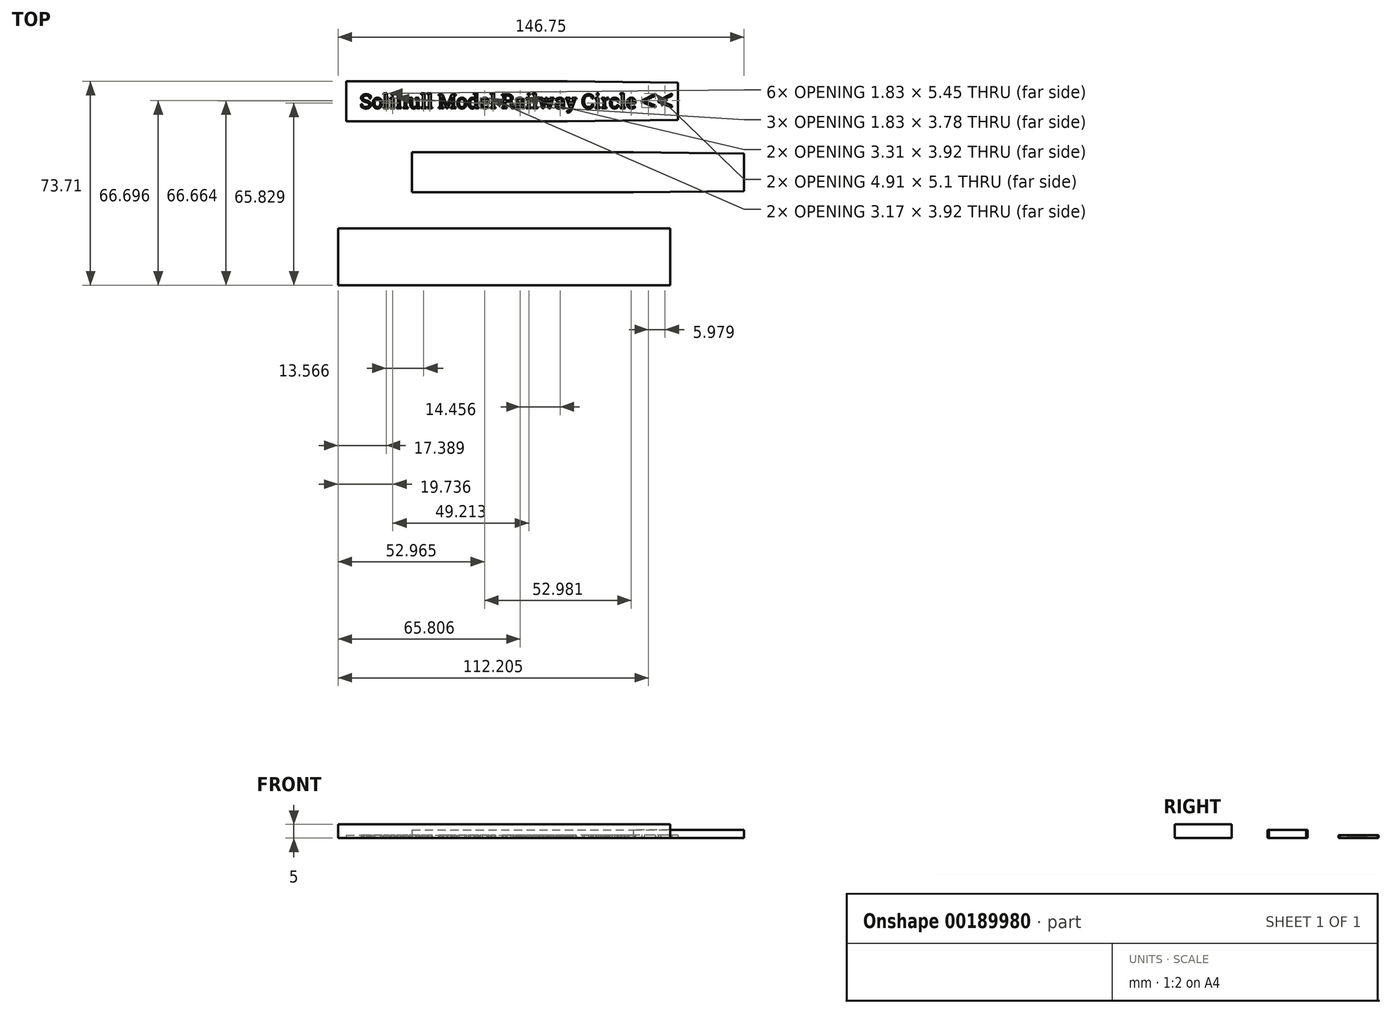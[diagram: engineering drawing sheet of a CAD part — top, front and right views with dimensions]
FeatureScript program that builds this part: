
annotation { "Feature Type Name" : "Feature", "Feature Type Description" : "" }
export const myFeature = defineFeature(function(context is Context, id is Id, definition is map)
    precondition{}
    {
        {
            var Q0;
            Q0=qCreatedBy(makeId("Top.planeOp"),FACE);
            var sketch = newSketch(context, id + "F0", { "sketchPlane" : qUnion([Q0])});
            skLineSegment(sketch, "E0.bottom", {"start": v(-62.12, -39.2) * mm, "end": v(57.88, -39.2) * mm});
            skLineSegment(sketch, "E0.top", {"start": v(-62.12, -59.7) * mm, "end": v(57.88, -59.7) * mm});
            skLineSegment(sketch, "E0.left", {"start": v(-62.12, -39.2) * mm, "end": v(-62.12, -59.7) * mm});
            skLineSegment(sketch, "E0.right", {"start": v(57.88, -39.2) * mm, "end": v(57.88, -59.7) * mm});
            skSolve(sketch);
        }
        {
            var Q0;
            Q0=qCreatedBy(makeId("Top.planeOp"),FACE);
            var sketch = newSketch(context, id + "F1", { "sketchPlane" : qUnion([Q0]), "disableImprinting" : false});
            skLineSegment(sketch, "E1.bottom", {"start": v(-59.23, 14) * mm, "end": v(20.77, 14) * mm});
            skLineSegment(sketch, "E1.top", {"start": v(-59.23, -0.5) * mm, "end": v(20.77, -0.5) * mm});
            skLineSegment(sketch, "E1.left", {"start": v(-59.23, 14) * mm, "end": v(-59.23, -0.5) * mm});
            skLineSegment(sketch, "E2", {"start": v(20.77, 14) * mm, "end": v(60.77, 13.5) * mm});
            skLineSegment(sketch, "E3", {"start": v(60.77, 13.5) * mm, "end": v(60.77, 0) * mm});
            skLineSegment(sketch, "E4", {"start": v(60.77, 0) * mm, "end": v(20.77, -0.5) * mm});
            skText(sketch, "E5", { "text": "Solihull Model Railway Circle", "fontName": "RobotoSlab-Regular.ttf"});
            skText(sketch, "E6", { "text": "<<", "fontName": "OpenSans-Regular.ttf"});
            const initialGuessF1  = {"E5": [-0.05423, 0.00423, 1, 0, 0.00515], "E6": [0.0471, 0.0032, 1, 0, 0.00753]};
            skSetInitialGuess(sketch, initialGuessF1);
            skSolve(sketch);
        }
        {
            var Q0;
            Q0=makeQuery(id+"F0.imprint","IMPRINT",FACE,{"disambiguationData":[TD([[makeQuery(id+"F0.imprint","IMPRINT",EDGE,{"derivedFrom":sQuery(id+"F0.wireOp",EDGE,"E0.bottom")}),-1.0]])]});
            extrude(context, id + "F2", {"entities" : qUnion([Q0]), "flatOperationType" : FlatOperationType.REMOVE, "offsetDistance" : 25 * mm, "depth" : 5 * mm, "domain" : OperationDomain.MODEL});
        }
        {
            var Q0;
            Q0=qCreatedBy(makeId("Top.planeOp"),FACE);
            var sketch = newSketch(context, id + "F3", { "sketchPlane" : qUnion([Q0])});
            skLineSegment(sketch, "E7.bottom", {"start": v(-35.37, -11.67) * mm, "end": v(44.63, -11.67) * mm});
            skLineSegment(sketch, "E7.top", {"start": v(-35.37, -26.17) * mm, "end": v(44.63, -26.17) * mm});
            skLineSegment(sketch, "E7.left", {"start": v(-35.37, -11.67) * mm, "end": v(-35.37, -26.17) * mm});
            skLineSegment(sketch, "E8", {"start": v(44.63, -11.67) * mm, "end": v(84.63, -12.17) * mm});
            skLineSegment(sketch, "E9", {"start": v(84.63, -12.17) * mm, "end": v(84.63, -25.67) * mm});
            skLineSegment(sketch, "E10", {"start": v(84.63, -25.67) * mm, "end": v(44.63, -26.17) * mm});
            skSolve(sketch);
        }
        {
            var Q0;
            Q0=makeQuery(id+"F3.imprint","IMPRINT",FACE,{"disambiguationData":[TD([[makeQuery(id+"F3.imprint","IMPRINT",EDGE,{"derivedFrom":sQuery(id+"F3.wireOp",EDGE,"E7.bottom")}),-1.0]])]});
            extrude(context, id + "F4", {"entities" : qUnion([Q0]), "flatOperationType" : FlatOperationType.REMOVE, "offsetDistance" : 25 * mm, "depth" : 3 * mm, "domain" : OperationDomain.MODEL});
        }
        {
            var Q0;
            Q0=makeQuery(id+"F1.imprint","IMPRINT",FACE,{"disambiguationData":[TD([[makeQuery(id+"F1.imprint","IMPRINT",EDGE,{"derivedFrom":sQuery(id+"F1.wireOp",EDGE,"E5.sketch_text.stroke-551")}),1.0]])]});
            var Q1;
            Q1=makeQuery(id+"F1.imprint","IMPRINT",FACE,{"disambiguationData":[TD([[makeQuery(id+"F1.imprint","IMPRINT",EDGE,{"derivedFrom":sQuery(id+"F1.wireOp",EDGE,"E5.sketch_text.stroke-410")}),1.0]])]});
            var Q2;
            Q2=makeQuery(id+"F1.imprint","IMPRINT",FACE,{"disambiguationData":[TD([[makeQuery(id+"F1.imprint","IMPRINT",EDGE,{"derivedFrom":sQuery(id+"F1.wireOp",EDGE,"E5.sketch_text.stroke-321")}),1.0]])]});
            var Q3;
            Q3=makeQuery(id+"F1.imprint","IMPRINT",FACE,{"disambiguationData":[TD([[makeQuery(id+"F1.imprint","IMPRINT",EDGE,{"derivedFrom":sQuery(id+"F1.wireOp",EDGE,"E5.sketch_text.stroke-287")}),1.0]])]});
            var Q4;
            Q4=makeQuery(id+"F1.imprint","IMPRINT",FACE,{"disambiguationData":[TD([[makeQuery(id+"F1.imprint","IMPRINT",EDGE,{"derivedFrom":sQuery(id+"F1.wireOp",EDGE,"E5.sketch_text.stroke-241")}),1.0]])]});
            var Q5;
            Q5=makeQuery(id+"F1.imprint","IMPRINT",FACE,{"disambiguationData":[TD([[makeQuery(id+"F1.imprint","IMPRINT",EDGE,{"derivedFrom":sQuery(id+"F1.wireOp",EDGE,"E5.sketch_text.stroke-214")}),1.0]])]});
            var Q6;
            Q6=makeQuery(id+"F1.imprint","IMPRINT",FACE,{"disambiguationData":[TD([[makeQuery(id+"F1.imprint","IMPRINT",EDGE,{"derivedFrom":sQuery(id+"F1.wireOp",EDGE,"E5.sketch_text.stroke-185")}),1.0]])]});
            var Q7;
            Q7=makeQuery(id+"F1.imprint","IMPRINT",FACE,{"disambiguationData":[TD([[makeQuery(id+"F1.imprint","IMPRINT",EDGE,{"derivedFrom":sQuery(id+"F1.wireOp",EDGE,"E5.sketch_text.stroke-40")}),1.0]])]});
            var Q8;
            Q8=makeQuery(id+"F1.imprint","IMPRINT",FACE,{"disambiguationData":[TD([[makeQuery(id+"F1.imprint","IMPRINT",EDGE,{"derivedFrom":sQuery(id+"F1.wireOp",EDGE,"E1.bottom")}),-1.0]])]});
            extrude(context, id + "F5", {"entities" : qUnion([Q0, Q1, Q2, Q3, Q4, Q5, Q6, Q7, Q8]), "depth" : 1 * mm});
        }
    });
